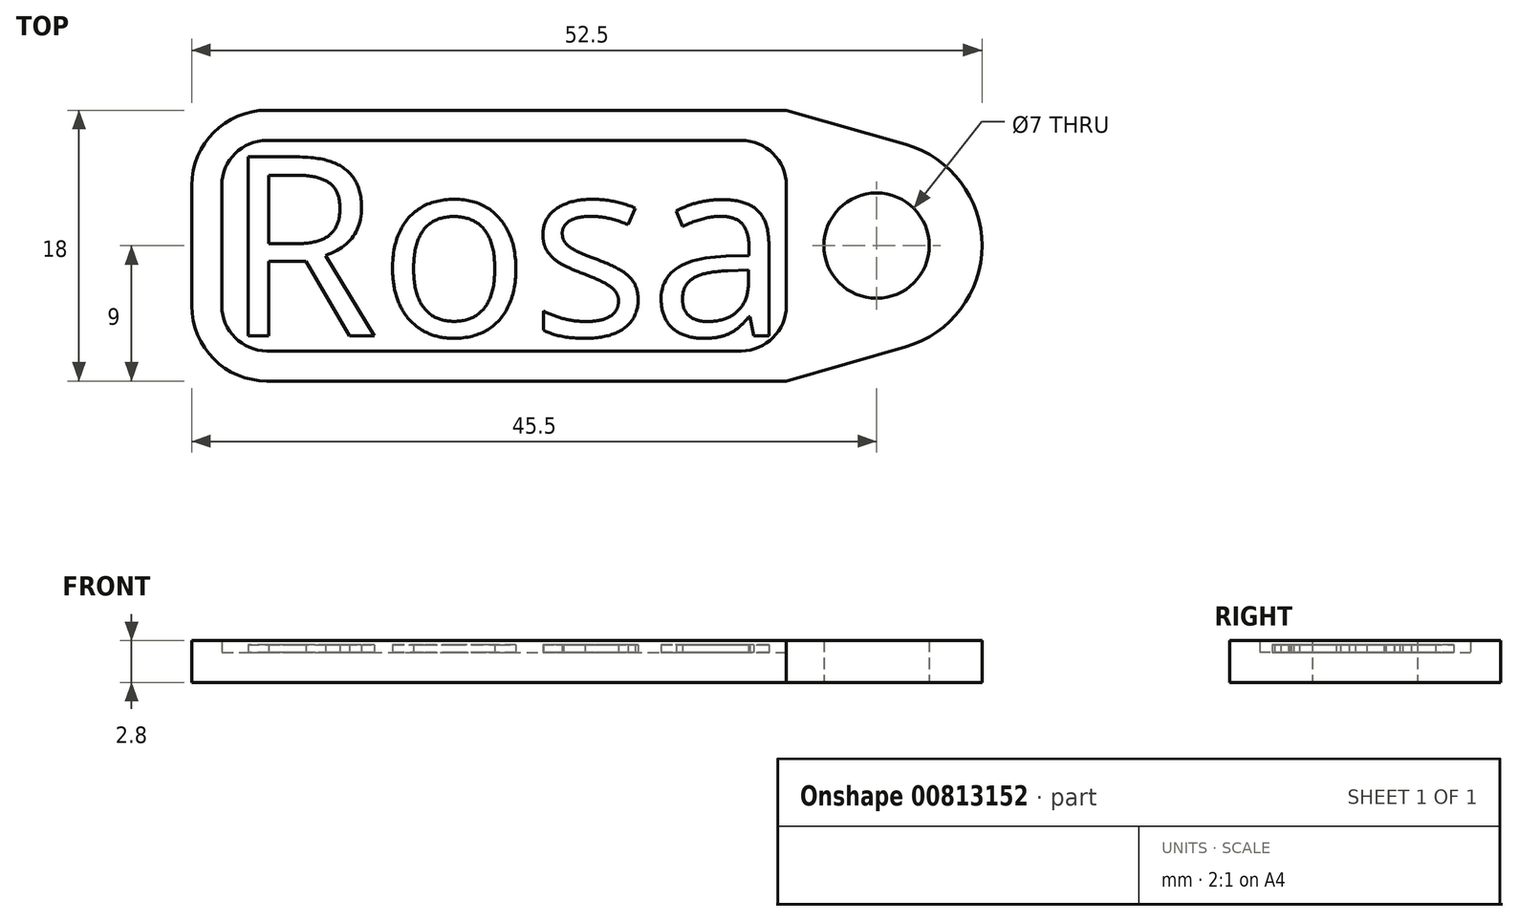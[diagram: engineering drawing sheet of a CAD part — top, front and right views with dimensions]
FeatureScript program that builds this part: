
annotation { "Feature Type Name" : "Feature", "Feature Type Description" : "" }
export const myFeature = defineFeature(function(context is Context, id is Id, definition is map)
    precondition{}
    {
        {
            var Q0;
            Q0=qCreatedBy(makeId("Top.planeOp"),FACE);
            var sketch = newSketch(context, id + "F0", { "sketchPlane" : qUnion([Q0])});
            skLineSegment(sketch, "E0", {"start": v(5, 9) * mm, "end": v(39.5, 9) * mm});
            skLineSegment(sketch, "E1", {"start": v(39.5, 9) * mm, "end": v(47.43, 6.73) * mm});
            skLineSegment(sketch, "E2", {"start": v(47.43, -6.73) * mm, "end": v(39.5, -9) * mm});
            skLineSegment(sketch, "E3", {"start": v(39.5, -9) * mm, "end": v(5, -9) * mm});
            skLineSegment(sketch, "E4", {"start": v(0, -4) * mm, "end": v(0, 4) * mm});
            skPoint(sketch, "E5.visualSharp", {"position": v(70.92, 0) * mm});
            skArc(sketch, "E5.filletArc", {"start": v(47.43, -6.73) * mm, "mid": v(52.5, 0) * mm, "end": v(47.43, 6.73) * mm});
            skPoint(sketch, "E6.visualSharp", {"position": v(0, 9) * mm});
            skArc(sketch, "E6.filletArc", {"start": v(5, 9) * mm, "mid": v(1.46, 7.54) * mm, "end": v(0, 4) * mm});
            skPoint(sketch, "E7.visualSharp", {"position": v(0, -9) * mm});
            skArc(sketch, "E7.filletArc", {"start": v(0, -4) * mm, "mid": v(1.46, -7.54) * mm, "end": v(5, -9) * mm});
            skSolve(sketch);
        }
        {
            var Q0;
            Q0=makeQuery(id+"F0.imprint","IMPRINT",FACE,{"disambiguationData":[TD([[makeQuery(id+"F0.imprint","IMPRINT",EDGE,{"derivedFrom":sQuery(id+"F0.wireOp",EDGE,"E0")}),-1.0]])]});
            extrude(context, id + "F1", {"entities" : qUnion([Q0]), "depth" : 2 * mm, "offsetDistance" : 25 * mm});
        }
        {
            var Q0;
            Q0=sQuery(id+"F0.wireOp",VERTEX,"E5.filletArc.center");
            var Q1;
            Q1=makeQuery(id+"F1.opExtrude","SWEPT_BODY",BODY,{"disambiguationData":[OSD([sQuery(id+"F0.wireOp",EDGE,"E0"),sQuery(id+"F0.wireOp",EDGE,"E1"),sQuery(id+"F0.wireOp",EDGE,"E2"),sQuery(id+"F0.wireOp",EDGE,"E3"),sQuery(id+"F0.wireOp",EDGE,"E4"),sQuery(id+"F0.wireOp",EDGE,"E5.filletArc"),sQuery(id+"F0.wireOp",EDGE,"E6.filletArc"),sQuery(id+"F0.wireOp",EDGE,"E7.filletArc")])]});
            hole(context, id + "F2", {"style" : HoleStyle.SIMPLE, "endStyle" : HoleEndStyle.THROUGH, "oppositeDirection" : true, "holeDiameter" : 7 * mm, "majorDiameter" : 5 * mm, "isTappedThrough" : true, "tappedDepth" : 12 * mm, "tapClearance" : 3, "locations" : qUnion([Q0]), "scope" : qUnion([Q1])});
        }
        {
            var Q0;
            Q0=makeQuery(id+"F1.opExtrude","CAP_FACE",FACE,{"disambiguationData":[OSD([sQuery(id+"F0.wireOp",EDGE,"E0"),sQuery(id+"F0.wireOp",EDGE,"E1"),sQuery(id+"F0.wireOp",EDGE,"E2"),sQuery(id+"F0.wireOp",EDGE,"E3"),sQuery(id+"F0.wireOp",EDGE,"E4"),sQuery(id+"F0.wireOp",EDGE,"E5.filletArc"),sQuery(id+"F0.wireOp",EDGE,"E6.filletArc"),sQuery(id+"F0.wireOp",EDGE,"E7.filletArc")])],"isStart":false});
            var sketch = newSketch(context, id + "F3", { "sketchPlane" : qUnion([Q0])});
            skLineSegment(sketch, "E8", {"start": v(2, 4) * mm, "end": v(2, -4) * mm});
            skLineSegment(sketch, "E9", {"start": v(5, -7) * mm, "end": v(36.5, -7) * mm});
            skLineSegment(sketch, "E10", {"start": v(39.5, -4) * mm, "end": v(39.5, 4) * mm});
            skLineSegment(sketch, "E11", {"start": v(36.5, 7) * mm, "end": v(5, 7) * mm});
            skPoint(sketch, "E12.visualSharp", {"position": v(2, 7) * mm});
            skArc(sketch, "E12.filletArc", {"start": v(5, 7) * mm, "mid": v(2.88, 6.12) * mm, "end": v(2, 4) * mm});
            skPoint(sketch, "E13.visualSharp", {"position": v(2, -7) * mm});
            skArc(sketch, "E13.filletArc", {"start": v(2, -4) * mm, "mid": v(2.88, -6.12) * mm, "end": v(5, -7) * mm});
            skPoint(sketch, "E14.visualSharp", {"position": v(39.5, -7) * mm});
            skArc(sketch, "E14.filletArc", {"start": v(36.5, -7) * mm, "mid": v(38.62, -6.12) * mm, "end": v(39.5, -4) * mm});
            skPoint(sketch, "E15.visualSharp", {"position": v(39.5, 7) * mm});
            skArc(sketch, "E15.filletArc", {"start": v(39.5, 4) * mm, "mid": v(38.62, 6.12) * mm, "end": v(36.5, 7) * mm});
            skText(sketch, "E16", { "text": "Rosa", "fontName": "OpenSans-Regular.ttf"});
            const initialGuessF3  = {"E16": [0.0021, -0.006, 1, 0, 0.012]};
            skSetInitialGuess(sketch, initialGuessF3);
            skSolve(sketch);
        }
        {
            var Q0;
            Q0=makeQuery(id+"F3.imprint","IMPRINT",FACE,{"disambiguationData":[TD([[makeQuery(id+"F3.imprint","IMPRINT",EDGE,{"derivedFrom":sQuery(id+"F3.wireOp",EDGE,"E16.sketch_text.stroke-0")}),-1.0]])]});
            var Q1;
            Q1=makeQuery(id+"F3.imprint","IMPRINT",FACE,{"disambiguationData":[TD([[makeQuery(id+"F3.imprint","IMPRINT",EDGE,{"derivedFrom":sQuery(id+"F3.wireOp",EDGE,"E16.sketch_text.stroke-18")}),-1.0]])]});
            var Q2;
            Q2=makeQuery(id+"F3.imprint","IMPRINT",FACE,{"disambiguationData":[TD([[makeQuery(id+"F3.imprint","IMPRINT",EDGE,{"derivedFrom":sQuery(id+"F3.wireOp",EDGE,"E16.sketch_text.stroke-35")}),-1.0]])]});
            var Q3;
            Q3=makeQuery(id+"F3.imprint","IMPRINT",FACE,{"disambiguationData":[TD([[makeQuery(id+"F3.imprint","IMPRINT",EDGE,{"derivedFrom":sQuery(id+"F3.wireOp",EDGE,"E16.sketch_text.stroke-60")}),-1.0]])]});
            extrude(context, id + "F4", {"entities" : qUnion([Q0, Q1, Q2, Q3]), "operationType" : NewBodyOperationType.ADD, "depth" : .5 * mm, "offsetDistance" : 25 * mm});
        }
        {
            var Q0;
            Q0=makeQuery(id+"F3.imprint","IMPRINT",FACE,{"disambiguationData":[TD([[makeQuery(id+"F3.imprint","IMPRINT",EDGE,{"derivedFrom":sQuery(id+"F3.wireOp",EDGE,"E8")}),-1.0]])]});
            extrude(context, id + "F5", {"entities" : qUnion([Q0]), "operationType" : NewBodyOperationType.ADD, "depth" : .8 * mm, "offsetDistance" : 25 * mm});
        }
    });
